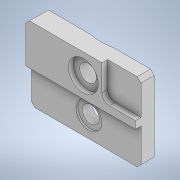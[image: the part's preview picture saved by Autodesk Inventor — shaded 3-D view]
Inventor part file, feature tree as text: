
AUTODESK INVENTOR PART (.ipt)
format: ipt  version: 2020 (Build 240168000, 168)  size: 248,320 bytes
history: native  units: in
note: dims shown in document units (in); Inventor stores cm internally (conversion verified against a paired STEP export)
features: sketch x9, extrude x7, hole x3, chamfer x1
ambient origin geometry x8: Origin, YZ Plane, XZ Plane, XY Plane, X Axis, Y Axis, Z Axis, Center Point
bodies: Solid1 (feature_tree)
feature tree (20):
  extrude  "Extrusion1"  Depth=0.8268in
  extrude  "Extrusion2"  Depth=0.3937in
  sketch  "Sketch3"  dims[d4=0.1398in d5=0.0in d6=1.1614in]
  hole  "Hole1"  [1 undecoded]
  hole  "Hole2"  [1 undecoded]
  sketch  "Sketch6"  dims[d12=0.0in d19=0.1772in]
  hole  "Hole3"  [1 undecoded]
  extrude  "Extrusion3"  TaperAngle=0.0deg  [1 undecoded]
  extrude  "Extrusion4"  Depth=0.4331in
  chamfer  "Chamfer3"  Distance=0.2165in
  extrude  "Extrusion5"  TaperAngle=0.0deg  [1 undecoded]
  extrude  "Extrusion6"  Depth=0.0787in
  extrude  "Extrusion7"  TaperAngle=0.0deg  [1 undecoded]
  sketch  "Sketch1"  dims[d0=1.1614in d1=0.8268in]
  sketch  "Sketch2"  dims[d2=0.3937in d3=0.5512in]
  sketch  "Sketch5"  dims[d8=0.0in d10=0.0591in d11=0.0in]
  sketch  "Sketch8"  dims[d20=0.1772in d21=0.328in d22=0.3126in d23=0.0197in d24=90.0deg d25=0.4843in d26=0.8108in d27=0.0in]
  sketch  "Sketch9"  dims[d28=0.4331in d29=0.2165in]
  sketch  "Sketch10"  dims[d30=0.1772in d31=0.328in d32=0.315in d33=0.0492in d34=90.0deg d35=0.4843in d36=0.8108in]
  sketch  "Sketch11"  dims[d37=0.0in d38=0.2165in d39=0.0in d40=0.1969in d41=0.0in d42=0.1969in d43=0.0827in d44=0.328in d45=0.2362in d46=0.0787in d47=90.0deg d48=0.0787in d49=0.0in d53=0.0in d54=0.0in d55=0.2756in d56=0.0197in d57=0.0in d58=0.0413in d60=0.0392in d61=0.0827in d62=0.0in d69=0.0394in d70=0.0787in d71=45.0deg d72=0.0in d73=1.0in d74=0.685in d75=0.3937in d76=0.0in d77=0.5512in d78=0.5512in d79=0.4134in d82=0.1476in d83=0.3353in d84=0.3543in d85=0.0in d86=0.0in d87=0.0in d88=0.3543in d89=0.0787in d90=0.0591in d91=0.0in d94=0.0787in d59=0.5635in d63=0.0295in d64=0.0148in d80=0.0059in d81=0.0098in d92=0.0197in d93=0.0344in d95=0.0344in]
note: 6 required parameter values undecoded (feature->parameter linkage not recoverable at this tier; creation-order binding heuristic only, values carry confidence <= 0.55)
